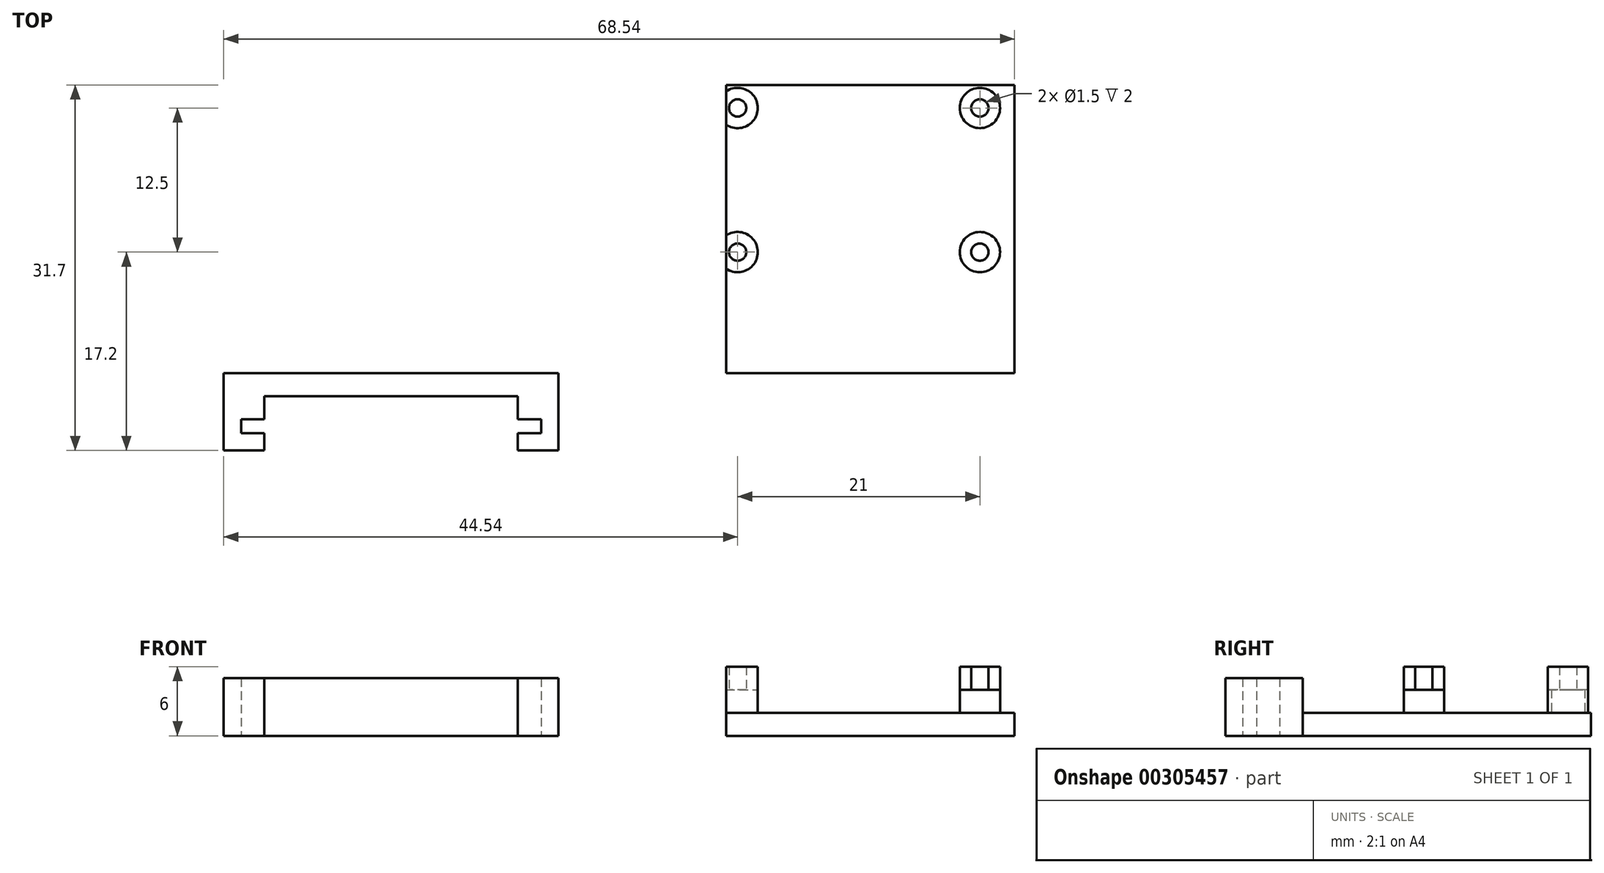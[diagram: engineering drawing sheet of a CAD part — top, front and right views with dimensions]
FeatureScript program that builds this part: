
annotation { "Feature Type Name" : "Feature", "Feature Type Description" : "" }
export const myFeature = defineFeature(function(context is Context, id is Id, definition is map)
    precondition{}
    {
        {
            var Q0;
            Q0=qCreatedBy(makeId("Top.planeOp"),FACE);
            var sketch = newSketch(context, id + "F0", { "sketchPlane" : qUnion([Q0])});
            skLineSegment(sketch, "E0.bottom", {"start": v(-11.5, 2) * mm, "end": v(13.5, 2) * mm});
            skLineSegment(sketch, "E0.top", {"start": v(-11.5, -23) * mm, "end": v(13.5, -23) * mm});
            skLineSegment(sketch, "E0.left", {"start": v(-11.5, 2) * mm, "end": v(-11.5, -23) * mm});
            skLineSegment(sketch, "E0.right", {"start": v(13.5, 2) * mm, "end": v(13.5, -23) * mm});
            skLineSegment(sketch, "E1", {"start": v(-10.5, 0) * mm, "end": v(10.5, 0) * mm, "construction": true});
            skLineSegment(sketch, "E2", {"start": v(-10.5, 0) * mm, "end": v(-10.5, -12.5) * mm, "construction": true});
            skCircle(sketch, "E3", {"center": v(-10.5, 0) * mm, "radius": 0.75 * mm});
            skCircle(sketch, "E4", {"center": v(-10.5, 0) * mm, "radius": 1.75 * mm});
            skPoint(sketch, "E5.startSnap0", {"position": v(13.5, -10.5) * mm});
            skPoint(sketch, "E5.endSnap0", {"position": v(-11.5, -10.5) * mm});
            skPoint(sketch, "E6", {"position": v(0, 0) * mm});
            skCircle(sketch, "E7.MirrorC", {"center": v(10.5, 0) * mm, "radius": 0.75 * mm});
            skCircle(sketch, "E8.MirrorC", {"center": v(10.5, 0) * mm, "radius": 1.75 * mm});
            skPoint(sketch, "E9", {"position": v(-10.5, -6.25) * mm});
            skLineSegment(sketch, "E10", {"start": v(-19.56, -6.25) * mm, "end": v(24.78, -6.25) * mm, "construction": true});
            skCircle(sketch, "E11.MirrorC", {"center": v(-10.5, -12.5) * mm, "radius": 0.75 * mm});
            skCircle(sketch, "E12.MirrorC", {"center": v(-10.5, -12.5) * mm, "radius": 1.75 * mm});
            skCircle(sketch, "E13.MirrorC", {"center": v(10.5, -12.5) * mm, "radius": 0.75 * mm});
            skCircle(sketch, "E14.MirrorC", {"center": v(10.5, -12.5) * mm, "radius": 1.75 * mm});
            skLineSegment(sketch, "E15", {"start": v(-40.54, -23) * mm, "end": v(-55.04, -23) * mm});
            skLineSegment(sketch, "E16", {"start": v(-55.04, -23) * mm, "end": v(-55.04, -29.7) * mm});
            skLineSegment(sketch, "E17", {"start": v(-55.04, -29.7) * mm, "end": v(-51.54, -29.7) * mm});
            skLineSegment(sketch, "E18", {"start": v(-51.54, -29.7) * mm, "end": v(-51.54, -28.2) * mm});
            skLineSegment(sketch, "E19", {"start": v(-51.54, -28.2) * mm, "end": v(-53.54, -28.2) * mm});
            skLineSegment(sketch, "E20", {"start": v(-53.54, -28.2) * mm, "end": v(-53.54, -27) * mm});
            skLineSegment(sketch, "E21", {"start": v(-53.54, -27) * mm, "end": v(-51.54, -27) * mm});
            skLineSegment(sketch, "E22", {"start": v(-51.54, -27) * mm, "end": v(-51.54, -25) * mm});
            skLineSegment(sketch, "E23", {"start": v(-51.54, -25) * mm, "end": v(-40.54, -25) * mm});
            skLineSegment(sketch, "E24", {"start": v(-40.54, -12.1) * mm, "end": v(-40.54, -37.5) * mm, "construction": true});
            skLineSegment(sketch, "E25.MirrorCS", {"start": v(-40.54, -23) * mm, "end": v(-26.04, -23) * mm});
            skLineSegment(sketch, "E26.MirrorCS", {"start": v(-26.04, -23) * mm, "end": v(-26.04, -29.7) * mm});
            skLineSegment(sketch, "E27.MirrorCS", {"start": v(-26.04, -29.7) * mm, "end": v(-29.54, -29.7) * mm});
            skLineSegment(sketch, "E28.MirrorCS", {"start": v(-29.54, -29.7) * mm, "end": v(-29.54, -28.2) * mm});
            skLineSegment(sketch, "E29.MirrorCS", {"start": v(-29.54, -28.2) * mm, "end": v(-27.54, -28.2) * mm});
            skLineSegment(sketch, "E30.MirrorCS", {"start": v(-27.54, -27) * mm, "end": v(-29.54, -27) * mm});
            skLineSegment(sketch, "E31.MirrorCS", {"start": v(-27.54, -28.2) * mm, "end": v(-27.54, -27) * mm});
            skLineSegment(sketch, "E32.MirrorCS", {"start": v(-29.54, -27) * mm, "end": v(-29.54, -25) * mm});
            skLineSegment(sketch, "E33.MirrorCS", {"start": v(-29.54, -25) * mm, "end": v(-40.54, -25) * mm});
            skSolve(sketch);
        }
        {
            var Q0;
            Q0=makeQuery(id+"F0.imprint","IMPRINT",FACE,{"disambiguationData":[TD([[makeQuery(id+"F0.imprint","IMPRINT",EDGE,{"derivedFrom":sQuery(id+"F0.wireOp",EDGE,"E0.bottom")}),-1.0]])]});
            extrude(context, id + "F1", {"entities" : qUnion([Q0]), "depth" : 2 * mm});
        }
        {
            var Q0;
            Q0=makeQuery(id+"F0.imprint","IMPRINT",FACE,{"disambiguationData":[TD([[makeQuery(id+"F0.imprint","IMPRINT",EDGE,{"derivedFrom":sQuery(id+"F0.wireOp",EDGE,"E3")}),-1.0]])]});
            var Q1;
            Q1=makeQuery(id+"F0.imprint","IMPRINT",FACE,{"disambiguationData":[TD([[makeQuery(id+"F0.imprint","IMPRINT",EDGE,{"derivedFrom":sQuery(id+"F0.wireOp",EDGE,"E7.MirrorC")}),1.0]])]});
            var Q2;
            Q2=makeQuery(id+"F0.imprint","IMPRINT",FACE,{"disambiguationData":[TD([[makeQuery(id+"F0.imprint","IMPRINT",EDGE,{"derivedFrom":sQuery(id+"F0.wireOp",EDGE,"E13.MirrorC")}),-1.0]])]});
            var Q3;
            Q3=makeQuery(id+"F0.imprint","IMPRINT",FACE,{"disambiguationData":[TD([[makeQuery(id+"F0.imprint","IMPRINT",EDGE,{"derivedFrom":sQuery(id+"F0.wireOp",EDGE,"E11.MirrorC")}),1.0]])]});
            extrude(context, id + "F2", {"entities" : qUnion([Q0, Q1, Q2, Q3]), "operationType" : NewBodyOperationType.ADD, "depth" : 4 * mm});
        }
        {
            var Q0;
            Q0=makeQuery(id+"F0.imprint","IMPRINT",FACE,{"disambiguationData":[TD([[makeQuery(id+"F0.imprint","IMPRINT",EDGE,{"derivedFrom":sQuery(id+"F0.wireOp",EDGE,"E3")}),1.0]])]});
            var Q1;
            Q1=makeQuery(id+"F0.imprint","IMPRINT",FACE,{"disambiguationData":[TD([[makeQuery(id+"F0.imprint","IMPRINT",EDGE,{"derivedFrom":sQuery(id+"F0.wireOp",EDGE,"E7.MirrorC")}),-1.0]])]});
            var Q2;
            Q2=makeQuery(id+"F0.imprint","IMPRINT",FACE,{"disambiguationData":[TD([[makeQuery(id+"F0.imprint","IMPRINT",EDGE,{"derivedFrom":sQuery(id+"F0.wireOp",EDGE,"E13.MirrorC")}),1.0]])]});
            var Q3;
            Q3=makeQuery(id+"F0.imprint","IMPRINT",FACE,{"disambiguationData":[TD([[makeQuery(id+"F0.imprint","IMPRINT",EDGE,{"derivedFrom":sQuery(id+"F0.wireOp",EDGE,"E11.MirrorC")}),-1.0]])]});
            extrude(context, id + "F3", {"entities" : qUnion([Q0, Q1, Q2, Q3]), "operationType" : NewBodyOperationType.ADD, "depth" : 6 * mm});
        }
        {
            var Q0;
            Q0=makeQuery(id+"F0.imprint","IMPRINT",FACE,{"disambiguationData":[TD([[makeQuery(id+"F0.imprint","IMPRINT",EDGE,{"derivedFrom":sQuery(id+"F0.wireOp",EDGE,"E15")}),1.0]])]});
            extrude(context, id + "F4", {"entities" : qUnion([Q0]), "depth" : 5 * mm});
        }
    });
